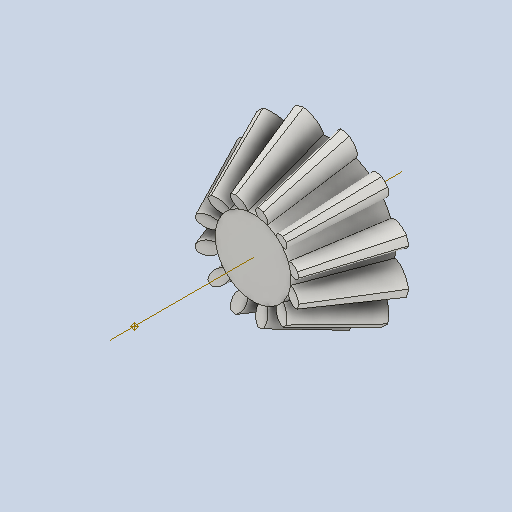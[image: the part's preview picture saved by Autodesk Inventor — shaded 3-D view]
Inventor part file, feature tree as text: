
AUTODESK INVENTOR PART (.ipt)
format: ipt  version: 2022 (Build 260153000, 153)  size: 487,424 bytes
history: native  units: mm
features: other x24, loft x2, pattern_circular x2, sketch x1
ambient origin geometry x6: Origin, XZ Plane, X Axis, Y Axis, Z Axis, Center Point
bodies: Solid1 (feature_tree)
feature tree (29):
  other  "Top Point"
  other  "Mesh Plane2"
  other  "Teeth Body"
  other  "Start Point"
  other  "Tooth Plane"
  other  "Start Sketch"
  other  "End Point"
  other  "3D Sketch Right"
  other  "End Plane Right"
  loft  "Loft Right"
  pattern_circular  "Circular Pattern Right"  [2 undecoded]
  other  "3D Sketch Left"
  other  "End Plane Left"
  loft  "Loft Left"
  pattern_circular  "Circular Pattern Left"  [2 undecoded]
  other  "Fix Body"
  other  "Mesh Plane"
  other  "Top Plane"
  other  "Teeth Body Sketch"
  other  "End Plane"
  other  "End Sketch"
  other  "Helical Curve Left"
  other  "End Sketch Left"
  other  "Body Sketch"
  sketch  "Sketch6"  dims[d0=24.0mm d1=19.543312mm d2=27.411178mm d3=12.9mm d4=29.317764mm d5=90.0deg d7=3.763947mm d8=5.032168mm d9=11.359554mm d11=13.111849mm d12=2.236532mm d15=2.990106mm d16=6.749829mm d17=0.0mm d18=90.0deg d19=0.0mm d20=90.0deg d21=120.0mm d22=360.0deg d26=153.94342mm d27=12.174046mm d28=24.0mm d29=-3.805064mm d30=2.236532mm d31=2.990106mm d32=6.749829mm d35=0.0mm d37=0.0mm d39=0.0mm d40=90.0deg d41=120.0mm d42=360.0deg d46=90.0deg d47=90.0deg d48=0.0mm d49=0.0mm d50=90.0deg d51=15.0deg d52=0.0mm d53=0.0mm d54=0.0mm d56=7.648649mm d57=16.032464mm d58=10.015958mm d59=9.526465mm d60=5.951467mm d61=9.526465mm d62=5.951467mm d63=90.0deg d64=90.0deg d65=153.94342mm d66=31.5mm d67=24.0mm d68=-3.805064mm d69=12.174046mm d70=2.990106mm d71=6.749829mm d72=2.236532mm d73=5.951467mm d74=9.526465mm d75=0.0mm d76=90.0deg d77=0.0mm d78=90.0deg d79=0.0mm d80=90.0deg d81=120.0mm d82=360.0deg d84=10.0mm d85=20.0mm d86=20.0mm d87=10.0mm d88=0.0mm d89=0.0mm]
  other  "Srf1"
  other  "Helical Curve Right"
  other  "End Sketch Right"
  other  "Pitch Diameter"
note: 4 required parameter values undecoded (feature->parameter linkage not recoverable at this tier; creation-order binding heuristic only, values carry confidence <= 0.55)
